# Revit family: Slat_Bench_BIM
name_source: partatom
category: Arredi
units: mm (PartAtom-declared; Revit-internal decimal feet)

## family parameters
Attiva taglio nelle viste = No
Basato su piano di lavoro = No
Condiviso = No
Numero OmniClass = 23.40.20.00
Origine composizione di rendering = Geometria famiglia
Punto di calcolo locali = No
Sempre verticale = Sì
Taglio con vuoti quando caricato = No
Titolo OmniClass = General Furniture and Specialties

## types (2) — shared parameters
AVAILABLE FINISHES = Ebonized black lacquer on Ash (EB) or bleached, white pigment, matte acrylic on Ash (BL). Raw effect lacquer on Oak (RE). Hand rubbed natural oil on Oak or Walnut (NA), or hand rubbed black oil on Walnut (BO).
BASE MATERIAL = BASSAM_FELLOWS_WALNUT_BLACK_OIL_W-BO
BIM BADGE = https://bim.archiproducts.com
COLLECTION = Slat
DEPTH = 406 mm  [stored 1.33202 ft]
Descrizione = Solid wood bench
HEIGHT = 406 mm  [stored 1.33202 ft]
MATERIAL DESCRIPTION = Carved solid wood slats. Upholstery: Foam with edge banding. Single topstitch detail.
PRODUCT SHEET = https://www.archiproducts.com
Produttore = BassamFellows
TECHNICAL SHEET = https://bassamfellows.com
UPHOLSTERY MATERIAL = <Per categoria>
URL = https://bassamfellows.com
zero-valued in all types: Prospetto di default

## per-type parameters (varying)
| type | CENTER LINE PILLOW | CENTRAL FEET | Modello | PILLOW LENGTH | PILLOW MATERIAL | WIDTH |
| CB-39L | 475 mm  [stored 1.5584 ft] | Sì | Slat Bench Long | 915 mm  [stored 3.00197 ft] | BASSAM_FELLOWS_ELEGANT_LEATHER_48027_OLIVE | 1930 mm |
| CB-39 | 1 mm  [stored 0.00328084 ft] | No | Slat Bench | 500 mm | BASSAM_FELLOWS_COMFORT_LEATHER_43632_CAMEL | 1220 mm  [stored 4.00262 ft] |

note: column(s) folded — value = type name in every type: PRODUCT CODE

note: [stored X ft] marks values corroborated as IEEE doubles in the binary element streams (Revit-internal decimal feet)

## geometry (parser evidence)
native form markers: Sweep x3
no freeform markers — native parametric forms only
